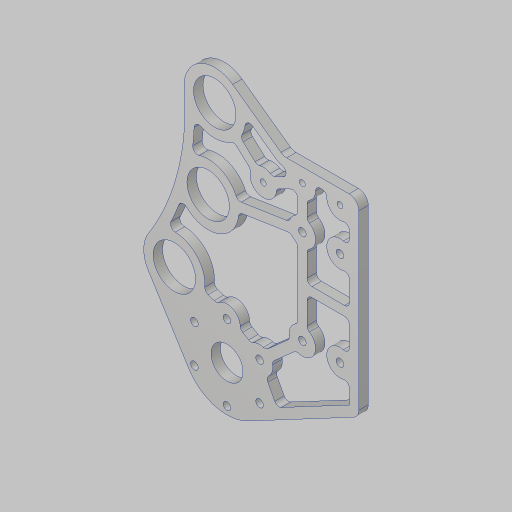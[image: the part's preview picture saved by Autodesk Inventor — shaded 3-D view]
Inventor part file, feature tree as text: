
AUTODESK INVENTOR PART (.ipt)
format: ipt  version: 2023.5 (Build 275446000, 446)  size: 473,088 bytes
history: native  units: in
note: dims shown in document units (in); Inventor stores cm internally (conversion verified against a paired STEP export)
features: sketch x4, hole x3, extrude x2, fillet x2, projected_geometry x2
ambient origin geometry x8: Origin, YZ Plane, XZ Plane, XY Plane, X Axis, Y Axis, Z Axis, Center Point
bodies: Solid1 (feature_tree)
feature tree (13):
  sketch  "Sketch1"  dims[d0=2.0in d1=15.0in]
  sketch  "Sketch2"  dims[d2=0.875in d3=17.0in d4=2.0in]
  extrude  "Extrusion1"  Depth=2.0in
  hole  "Hole1"  [1 undecoded]
  fillet  "Fillet1"  Radius=2.0in
  hole  "Hole2"  [1 undecoded]
  hole  "Hole3"  [1 undecoded]
  extrude  "Extrusion2"  Depth=0.25in
  fillet  "Fillet2"  Radius=3.6in
  sketch  "Sketch3"  dims[d5=17.0in d6=1.0in]
  projected_geometry  "Projected Loop1"
  sketch  "Sketch4"  dims[d7=0.2405in d8=2.4in d9=0.5in d10=3.6in d11=1.5in d12=1.5in d13=0.9in d14=3.7in d15=1.0in d16=3.4in d17=3.0in d20=2.0in d22=1.125in d23=4.297in d24=0.25in d25=2.0in d26=2.3622in d28=360.0deg d30=7.0in d31=2.0in d32=0.201in d33=1.0in d34=1.5in d35=1.0in d36=0.201in d37=1.0in d38=1.0in d39=2.5in d40=0.25in d41=0.0in d42=0.85in d43=0.201in d44=0.75in d45=0.385in d46=0.25in d47=0.5635in d48=1.0in d49=0.8108in d50=0.375in d51=0.26in d52=1.825in d53=0.156in d54=0.38in d55=0.385in d56=0.25in d57=0.5635in d58=1.0in d59=0.8108in d60=0.25in d61=0.25in d62=0.25in d63=0.25in d64=0.25in d65=0.25in d66=0.125in d67=0.125in d68=0.125in d69=0.125in d70=2.5in d71=0.125in d72=0.125in d73=0.125in d74=0.125in d75=1.0in d76=0.0in d77=0.0in d78=0.13in d81=1.75in d82=0.875in d83=0.156in d84=0.38in d85=0.375in d86=0.25in d87=0.5635in d88=1.0in d89=0.8108in d90=0.125in d91=0.125in]
  projected_geometry  "Projected Loop2"
note: 3 required parameter values undecoded (feature->parameter linkage not recoverable at this tier; creation-order binding heuristic only, values carry confidence <= 0.55)
